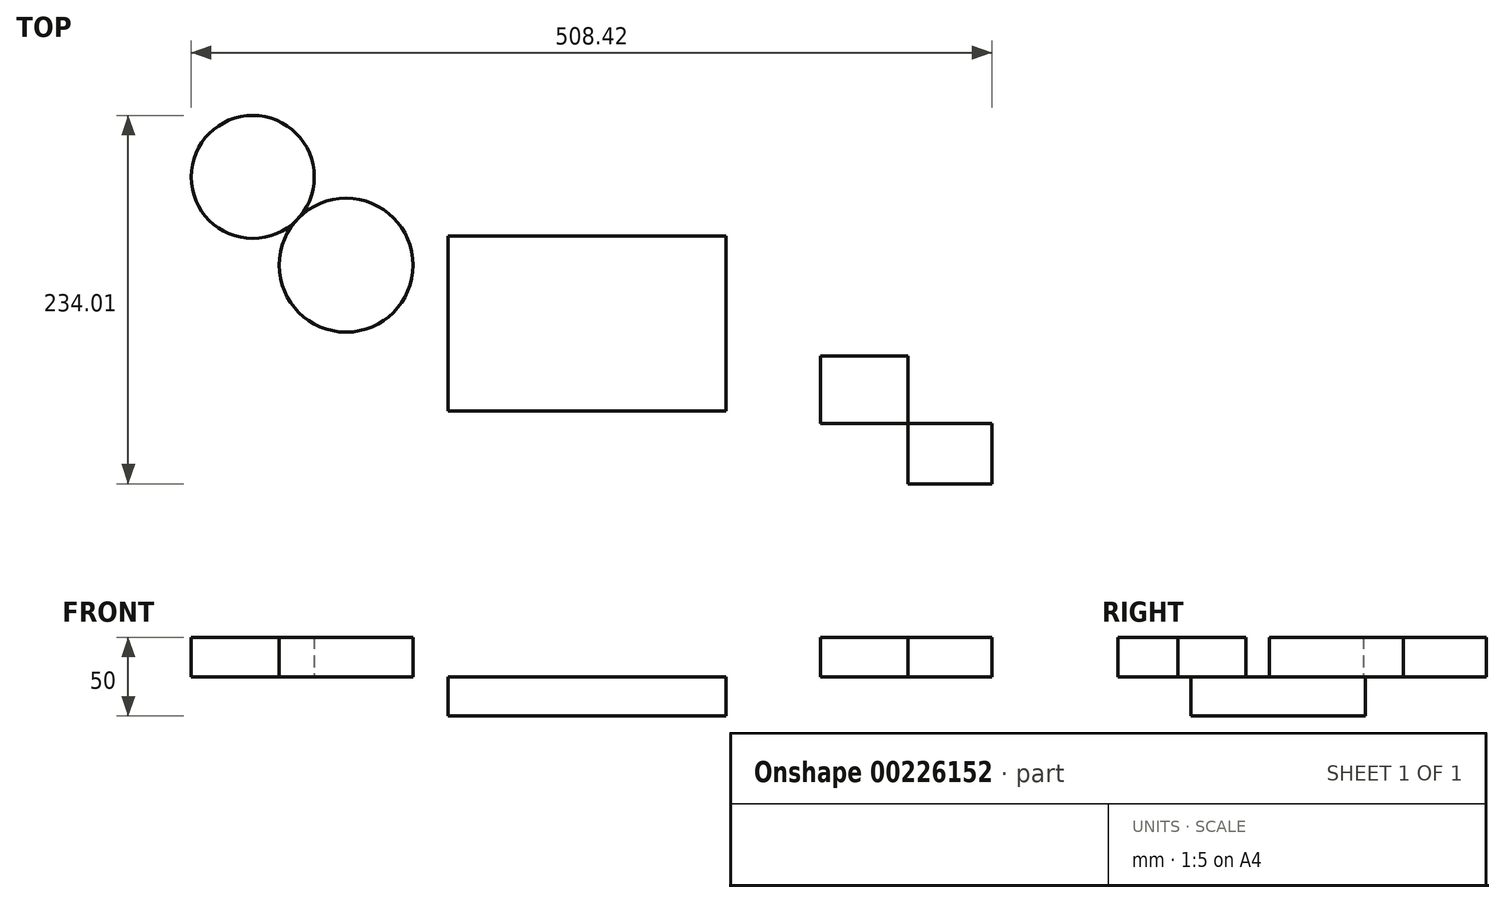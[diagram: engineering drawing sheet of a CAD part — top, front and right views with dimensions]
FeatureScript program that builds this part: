
annotation { "Feature Type Name" : "Feature", "Feature Type Description" : "" }
export const myFeature = defineFeature(function(context is Context, id is Id, definition is map)
    precondition{}
    {
        {
            var Q0;
            Q0=qCreatedBy(makeId("Top.planeOp"),FACE);
            var sketch = newSketch(context, id + "F0", { "sketchPlane" : qUnion([Q0])});
            skLineSegment(sketch, "E0.bottom", {"start": v(88.32, 55.45) * mm, "end": v(-88.32, 55.45) * mm});
            skLineSegment(sketch, "E0.top", {"start": v(88.32, -55.45) * mm, "end": v(-88.32, -55.45) * mm});
            skLineSegment(sketch, "E0.left", {"start": v(88.32, 55.45) * mm, "end": v(88.32, -55.45) * mm});
            skLineSegment(sketch, "E0.right", {"start": v(-88.32, 55.45) * mm, "end": v(-88.32, -55.45) * mm});
            skPoint(sketch, "E0.middle", {"position": v(0, 0) * mm});
            skSolve(sketch);
        }
        {
            var Q0;
            Q0 = qSketchRegion(id + "F0", true);
            extrude(context, id + "F1", {"entities" : qUnion([Q0]), "oppositeDirection" : true, "depth" : 25 * mm});
        }
        {
            var Q0;
            Q0=qCreatedBy(makeId("Top.planeOp"),FACE);
            var sketch = newSketch(context, id + "F2", { "sketchPlane" : qUnion([Q0])});
            skLineSegment(sketch, "E1.bottom", {"start": v(148.4, -20.54) * mm, "end": v(203.98, -20.54) * mm});
            skLineSegment(sketch, "E1.top", {"start": v(148.4, -63.56) * mm, "end": v(203.98, -63.56) * mm});
            skLineSegment(sketch, "E1.left", {"start": v(148.4, -20.54) * mm, "end": v(148.4, -63.56) * mm});
            skLineSegment(sketch, "E1.right", {"start": v(203.98, -20.54) * mm, "end": v(203.98, -63.56) * mm});
            skLineSegment(sketch, "E2.bottom", {"start": v(203.98, -63.56) * mm, "end": v(257.16, -63.56) * mm});
            skLineSegment(sketch, "E2.top", {"start": v(203.98, -101.8) * mm, "end": v(257.16, -101.8) * mm});
            skLineSegment(sketch, "E2.left", {"start": v(203.98, -63.56) * mm, "end": v(203.98, -101.8) * mm});
            skLineSegment(sketch, "E2.right", {"start": v(257.16, -63.56) * mm, "end": v(257.16, -101.8) * mm});
            skSolve(sketch);
        }
        {
            var Q0;
            Q0 = qSketchRegion(id + "F2", true);
            extrude(context, id + "F3", {"entities" : qUnion([Q0]), "depth" : 25 * mm});
        }
        {
            var Q0;
            Q0=qCreatedBy(makeId("Top.planeOp"),FACE);
            var sketch = newSketch(context, id + "F4", { "sketchPlane" : qUnion([Q0])});
            skCircle(sketch, "E3", {"center": v(-212.19, 93.13) * mm, "radius": 39.07 * mm});
            skCircle(sketch, "E4", {"center": v(-152.9, 37.08) * mm, "radius": 42.52 * mm});
            skSolve(sketch);
        }
        {
            var Q0;
            Q0 = qSketchRegion(id + "F4", true);
            extrude(context, id + "F5", {"entities" : qUnion([Q0]), "depth" : 25 * mm});
        }
    });
